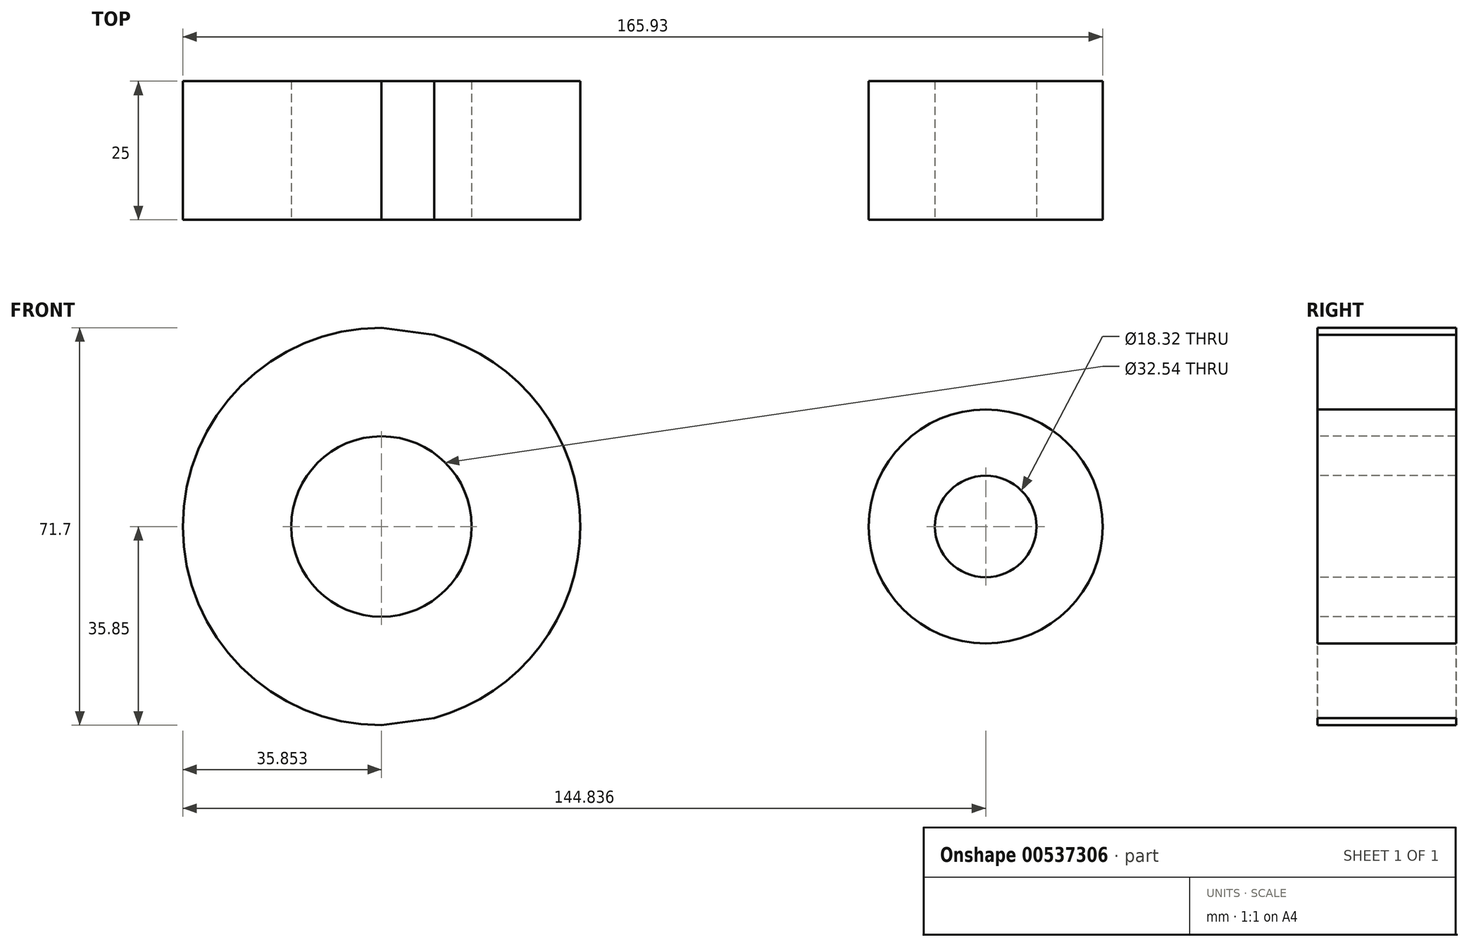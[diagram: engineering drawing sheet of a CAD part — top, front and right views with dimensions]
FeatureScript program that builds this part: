
annotation { "Feature Type Name" : "Feature", "Feature Type Description" : "" }
export const myFeature = defineFeature(function(context is Context, id is Id, definition is map)
    precondition{}
    {
        {
            var Q0;
            Q0=qCreatedBy(makeId("Front.planeOp"),FACE);
            var sketch = newSketch(context, id + "F0", { "sketchPlane" : qUnion([Q0])});
            skCircle(sketch, "E0", {"center": v(-50.29, 0) * mm, "radius": 35.85 * mm});
            skCircle(sketch, "E1", {"center": v(-50.29, 0) * mm, "radius": 16.27 * mm});
            skCircle(sketch, "E2", {"center": v(58.7, 0) * mm, "radius": 21.1 * mm});
            skCircle(sketch, "E3", {"center": v(58.7, 0) * mm, "radius": 9.16 * mm});
            skLineSegment(sketch, "E4", {"start": v(-50.29, 35.85) * mm, "end": v(58.7, 21.1) * mm});
            skLineSegment(sketch, "E5", {"start": v(-50.29, -35.85) * mm, "end": v(58.7, -21.1) * mm});
            skSolve(sketch);
        }
        {
            var Q0;
            Q0=makeQuery(id+"F0.imprint","IMPRINT",FACE,{"disambiguationData":[TD([[makeQuery(id+"F0.imprint","IMPRINT",EDGE,{"derivedFrom":sQuery(id+"F0.wireOp",EDGE,"E1")}),-1.0]])]});
            var Q1;
            Q1=makeQuery(id+"F0.imprint","IMPRINT",FACE,{"disambiguationData":[TD([[makeQuery(id+"F0.imprint","IMPRINT",EDGE,{"derivedFrom":sQuery(id+"F0.wireOp",EDGE,"E3")}),-1.0]])]});
            var Q2;
            {var subQ0=sQuery(id+"F0.wireOp",EDGE,"E4");var subQ1=sQuery(id+"F0.wireOp",EDGE,"E0");var subQ2=makeQuery(id+"F0.imprint","INTERSECT",VERTEX,{"disambiguationData":[OD(1.0)],"derivedFrom":[subQ1,subQ0]});Q2=makeQuery(id+"F0.imprint","IMPRINT",FACE,{"disambiguationData":[TD([[makeQuery(id+"F0.imprint","IMPRINT",EDGE,{"disambiguationData":[TD([[subQ2,1.0]])],"derivedFrom":subQ1}),-1.0]])]});}
            extrude(context, id + "F1", {"entities" : qUnion([Q0, Q1, Q2]), "oppositeDirection" : true, "depth" : 25 * mm, "offsetDistance" : 25.4 * mm});
        }
        {
            var Q0;
            Q0=qCreatedBy(makeId("Front.planeOp"),FACE);
            var sketch = newSketch(context, id + "F2", { "sketchPlane" : qUnion([Q0])});
            skCircle(sketch, "E6", {"center": v(-50.15, 0) * mm, "radius": 22.47 * mm});
            skSolve(sketch);
        }
        {
            var Q0;
            Q0=qCreatedBy(makeId("Front.planeOp"),FACE);
            var sketch = newSketch(context, id + "F3", { "sketchPlane" : qUnion([Q0])});
            skCircle(sketch, "E7", {"center": v(-50.08, 0) * mm, "radius": 17.79 * mm});
            skSolve(sketch);
        }
        {
            var Q0;
            Q0=sQuery(id+"F3.wireOp",EDGE,"E7");
            var Q1;
            Q1=sQuery(id+"F2.wireOp",EDGE,"E6");
            extrude(context, id + "F4", {"bodyType" : ToolBodyType.SURFACE, "surfaceEntities" : qUnion([Q0, Q1]), "depth" : 25.4 * mm, "offsetDistance" : 25.4 * mm});
        }
    });
